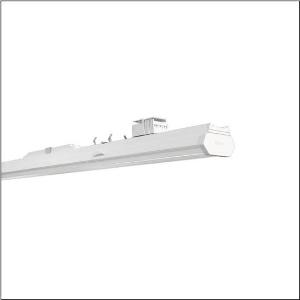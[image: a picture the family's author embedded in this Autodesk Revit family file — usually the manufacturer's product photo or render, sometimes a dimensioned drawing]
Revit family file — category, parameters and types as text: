
# Revit family: licross_r__21_protected_ho_52td12dn4e5md_1fe0
name_source: partatom
category: Lighting Fixtures
units: mm (PartAtom-declared; Revit-internal decimal feet)

## family parameters
Cut with Voids When Loaded = No
Host = Face
Light Source = No
Part Type = Normal
Room Calculation Point = No
Round Connector Dimension = Use Diameter
Shared = No

## types (1)
- --- (1 x LED, 2200 lm, 14.2 W, 4000K)
    Apparent Load = 14 VA
    CIE Flux Codes = 70 91 97 98 100
    Color Rendering = 80
    Color Temperature = 4000K
    Default Elevation = 1800 mm
    Description = Licross® 21 Protected HO, luminaire insert, of sheet steel, galvanised, coil coated, white, length: 1.500mm, width: 90mm, height: 103mm, LED rated luminous flux: 14.690lm, light colour: 840, control gear: DALI 2, with plug, 6-pole, with phase selection, mains connection: 220..240V, AC/DC, 0/50..60Hz, rated input power: 85W, without changeover relay, for emergency light function, for central battery installations according to DIN EN 60598-2-22, halogen-free wiring, primary light control with lens, of plastic, primary optical cover: cover, of PMMA, light emission: direct distribution, primary light characteristic: symmetric, protection rating (complete): IP54, insulation class (complete): insulation class I (protective earthing), certification: CE, ENEC, VDE, UKCA, protection symbol: D if used in an environment with non-conductive dust loads with corresponding accessories, impact resistance: IK06, permissible ambient temperature for indoor applications: -25..+35°C, standard: EN 60598-2-22, corresponds to IFS (International Featured Standards) requirements for safety and quality in the food industry, reducing of maximum allowable ambient temperature of 5°C with ceiling mounting, LABS conformity tested according to VDMA 24364:2018-05, packaging unit: 1 piece
    Height = 92 mm
    Lamp = 1 x LED
    Lamp Light Flux = 2200 lm
    Lamp Power = 14.2 W
    Lamp count = 1
    Length = 1500 mm
    Luminous efficacy = 155 lm/W
    Manufacturer = Siteco
    ModVariant = No
    Model = 52TD12DN4E5MD
    Mounting Place = Ceiling
    Mounting Type = Pendant
    Number of Poles = 1
    OnlyDefault = Yes
    Power Factor = 1
    Product Name = Licross® 21 Protected HO
    Product group = luminaire insert
    ProductGroupID = 901
    Protection Class = Protection class I
    Protection Degree = IP 54
    RLX_Detail_Level = 1
    RLX_Emergency_Light_Flux = 0 lm
    RLX_Emergency_Type = 0
    RLX_Emergency_Type_DB = No
    RlxData = <blob elided: 24933 chars, md5=340ffaac>
    Socket = socket
    Standby Power = 0 W
    System Light Flux = 2200 lm
    System Power = 14 W
    Type Comments = : DC mode (central or group accumulator) initial emergency light level
    Type Image = l_1256148.jpg
    URL = http://relux.com
    VarID = @adj_046387
    Voltage = 0 V
    Weight = 0.00 kg
    Width = 88 mm

## geometry (parser evidence)
native form markers: Blend x4, Sweep x10
no freeform markers — native parametric forms only
